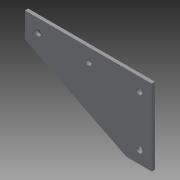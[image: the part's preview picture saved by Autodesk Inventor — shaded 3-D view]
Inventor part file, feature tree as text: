
AUTODESK INVENTOR PART (.ipt)
format: ipt  version: 2013 (Build 170138000, 138)  size: 105,984 bytes
history: native  units: in
note: dims shown in document units (in); Inventor stores cm internally (conversion verified against a paired STEP export)
features: extrude x2, sketch x2, plane x1
ambient origin geometry x8: Origin, YZ Plane, XZ Plane, XY Plane, X Axis, Y Axis, Z Axis, Center Point
bodies: Solid1 (feature_tree)
feature tree (5):
  plane  "Work Plane1"
  extrude  "Extrusion1"  Depth=1.0in
  extrude  "Extrusion2"  Depth=1.0in
  sketch  "Sketch1"  dims[d0=26.5in d1=1.0in]
  sketch  "Sketch2"  dims[d2=10.0in d3=1.0in d4=1.0in d5=5.0in d6=5.0in d7=1.0in d14=0.25in d15=0.25in d16=0.25in d17=0.25in d20=0.25in d21=0.125in d22=0.0in d23=1.0in d24=3.0in d25=1.0in d26=0.0in]
